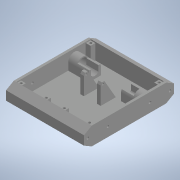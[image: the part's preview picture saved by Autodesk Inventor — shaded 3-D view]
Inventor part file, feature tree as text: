
AUTODESK INVENTOR PART (.ipt)
format: ipt  version: 2020 (Build 240168000, 168)  size: 381,440 bytes
history: native  units: in
note: dims shown in document units (in); Inventor stores cm internally (conversion verified against a paired STEP export)
features: projected_geometry x13, extrude x11, sketch x11, mirror x4, plane x1
ambient origin geometry x8: Origin, YZ Plane, XZ Plane, XY Plane, X Axis, Y Axis, Z Axis, Center Point
bodies: Solid1 (feature_tree)
feature tree (40):
  extrude  "Extrusion1"  Depth=5.9055in
  extrude  "Extrusion2"  TaperAngle=0.0deg  [1 undecoded]
  extrude  "Extrusion3"  Depth=1.063in
  extrude  "Extrusion4"  Depth=0.315in
  extrude  "Extrusion5"  TaperAngle=0.0deg  [1 undecoded]
  extrude  "Extrusion6"  Depth=0.5906in
  mirror  "Mirror1"
  extrude  "Extrusion7"  Depth=0.0787in
  mirror  "Mirror2"
  extrude  "Extrusion8"  Depth=0.5512in
  mirror  "Mirror3"
  plane  "Work Plane1"
  extrude  "Extrusion9"  Depth=0.7874in TaperAngle=0.0deg
  mirror  "Mirror4"
  extrude  "Extrusion10"  Depth=6.063in TaperAngle=0.0deg
  extrude  "Extrusion11"  Depth=0.1575in
  sketch  "Sketch1"  dims[d0=1.1811in d1=5.9055in]
  sketch  "Sketch2"  dims[d2=5.1181in d3=0.0in]
  projected_geometry  "Projected Loop1"
  sketch  "Sketch3"  dims[d4=0.1575in d5=1.063in]
  projected_geometry  "Projected Loop2"
  projected_geometry  "Projected Loop3"
  sketch  "Sketch4"  dims[d6=0.0in d8=0.315in]
  sketch  "Sketch5"  dims[d10=0.993in d11=0.0in]
  projected_geometry  "Projected Loop4"
  sketch  "Sketch6"  dims[d12=0.6496in d13=0.5906in]
  sketch  "Sketch7"  dims[d14=1.5748in d15=0.0787in]
  sketch  "Sketch9"  dims[d16=0.5512in d17=0.0in d18=0.6102in]
  sketch  "Sketch10"  dims[d19=0.4803in d20=0.7874in d21=0.0in]
  sketch  "Sketch12"  dims[d22=0.1654in d23=6.063in d24=0.0in]
  projected_geometry  "Projected Loop6"
  projected_geometry  "Projected Loop7"
  projected_geometry  "Projected Loop8"
  sketch  "Sketch13"  dims[d25=0.5114in d26=0.1575in d27=1.5748in d28=0.0in d29=0.0in d30=0.1575in d31=0.2756in d32=0.0in d33=0.4331in d34=0.122in d38=2.7559in d40=0.061in d41=0.0909in d42=0.2362in d43=0.0in d44=60.0deg d45=0.0787in d46=0.315in d48=0.993in d49=0.0in d51=0.1575in d52=0.1575in d53=0.2756in d54=0.0in]
  projected_geometry  "Projected Loop9"
  projected_geometry  "Projected Loop10"
  projected_geometry  "Projected Loop11"
  projected_geometry  "Projected Loop12"
  projected_geometry  "Projected Loop13"
  projected_geometry  "Projected Loop14"
note: 2 required parameter values undecoded (feature->parameter linkage not recoverable at this tier; creation-order binding heuristic only, values carry confidence <= 0.55)
